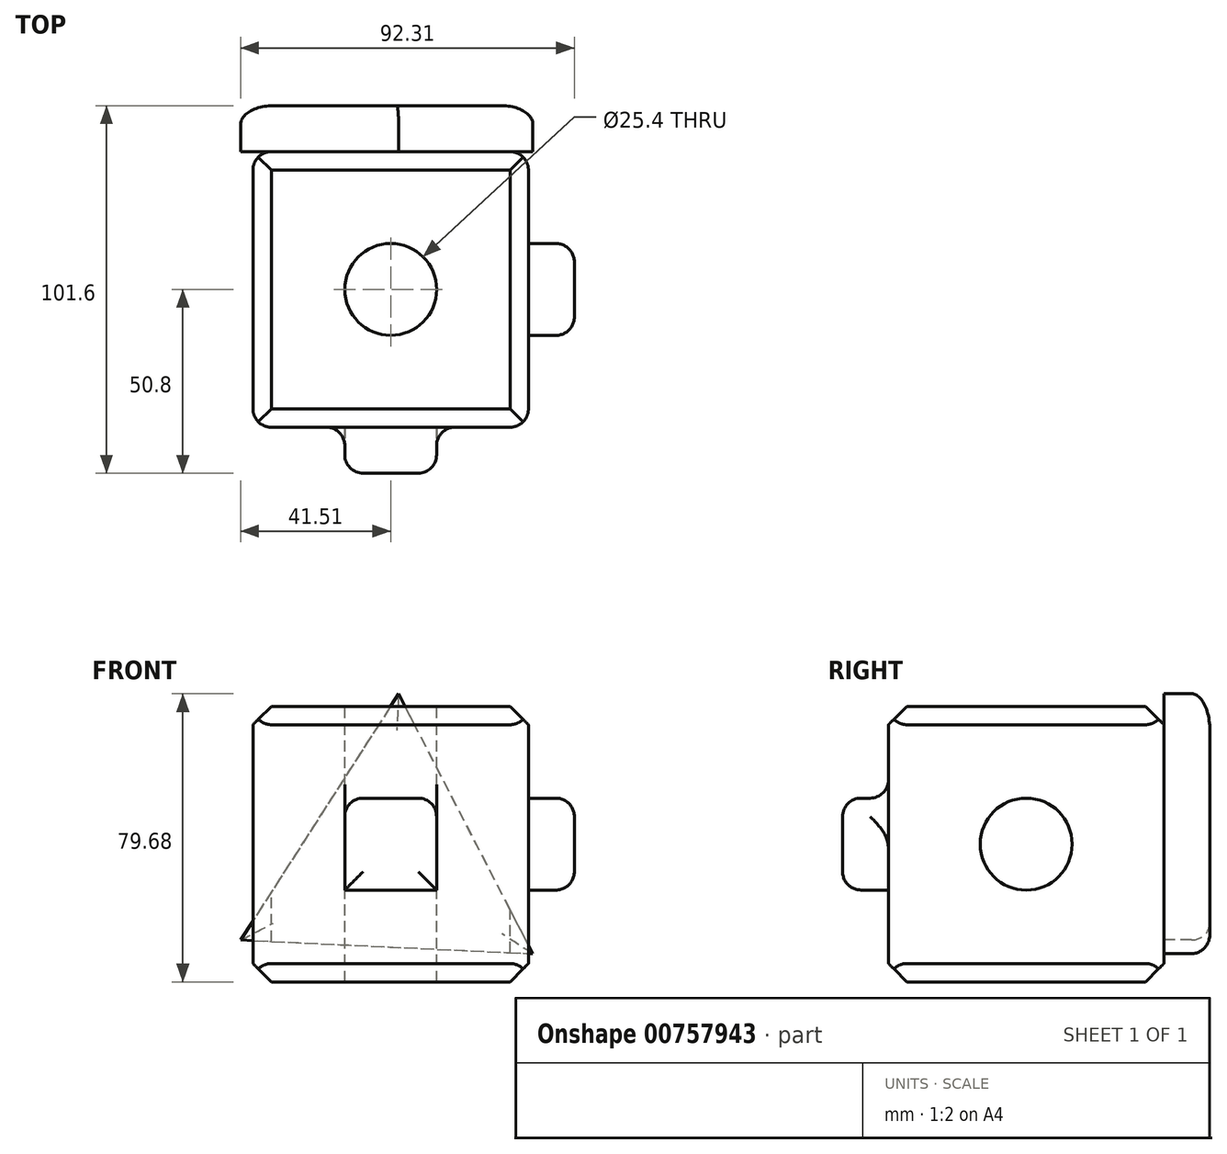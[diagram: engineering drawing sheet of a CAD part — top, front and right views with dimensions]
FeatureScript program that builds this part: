
annotation { "Feature Type Name" : "Feature", "Feature Type Description" : "" }
export const myFeature = defineFeature(function(context is Context, id is Id, definition is map)
    precondition{}
    {
        {
            var Q0;
            Q0=qCreatedBy(makeId("Front.planeOp"),FACE);
            var sketch = newSketch(context, id + "F0", { "sketchPlane" : qUnion([Q0])});
            skLineSegment(sketch, "E0.bottom", {"start": v(0, 32.56) * mm, "end": v(76.2, 32.56) * mm});
            skLineSegment(sketch, "E0.top", {"start": v(0, 108.76) * mm, "end": v(76.2, 108.76) * mm});
            skLineSegment(sketch, "E0.left", {"start": v(0, 32.56) * mm, "end": v(0, 108.76) * mm});
            skLineSegment(sketch, "E0.right", {"start": v(76.2, 32.56) * mm, "end": v(76.2, 108.76) * mm});
            skSolve(sketch);
        }
        {
            var Q0;
            Q0=makeQuery(id+"F0.imprint","IMPRINT",FACE,{"disambiguationData":[TD([[makeQuery(id+"F0.imprint","IMPRINT",EDGE,{"derivedFrom":sQuery(id+"F0.wireOp",EDGE,"E0.bottom")}),1.0]])]});
            extrude(context, id + "F1", {"entities" : qUnion([Q0]), "depth" : 76.2 * mm, "offsetDistance" : 25.4 * mm});
        }
        {
            var Q0;
            Q0=makeQuery(id+"F1.opExtrude","SWEPT_FACE",FACE,{"disambiguationData":[OSD([sQuery(id+"F0.wireOp",EDGE,"E0.top")])]});
            var sketch = newSketch(context, id + "F2", { "sketchPlane" : qUnion([Q0])});
            skPoint(sketch, "E1", {"position": v(38.1, -38.1) * mm});
            skSolve(sketch);
        }
        {
            var Q0;
            Q0=sQuery(id+"F2.wireOp",VERTEX,"E1");
            var Q1;
            Q1=makeQuery(id+"F1.opExtrude","SWEPT_BODY",BODY,{"disambiguationData":[OSD([sQuery(id+"F0.wireOp",EDGE,"E0.bottom"),sQuery(id+"F0.wireOp",EDGE,"E0.top"),sQuery(id+"F0.wireOp",EDGE,"E0.left"),sQuery(id+"F0.wireOp",EDGE,"E0.right")])]});
            hole(context, id + "F3", {"style" : HoleStyle.SIMPLE, "endStyle" : HoleEndStyle.THROUGH, "holeDiameter" : 25.4 * mm, "majorDiameter" : 6.35 * mm, "isTappedThrough" : true, "tappedDepth" : 12.7 * mm, "tapClearance" : 3, "locations" : qUnion([Q0]), "scope" : qUnion([Q1])});
        }
        {
            var Q0;
            Q0=makeQuery(id+"F1.opExtrude","CAP_FACE",FACE,{"disambiguationData":[OSD([sQuery(id+"F0.wireOp",EDGE,"E0.bottom"),sQuery(id+"F0.wireOp",EDGE,"E0.top"),sQuery(id+"F0.wireOp",EDGE,"E0.left"),sQuery(id+"F0.wireOp",EDGE,"E0.right")])],"isStart":false});
            var sketch = newSketch(context, id + "F4", { "sketchPlane" : qUnion([Q0])});
            skPoint(sketch, "E2", {"position": v(38.1, 70.66) * mm});
            skLineSegment(sketch, "E3.bottom", {"start": v(25.4, 83.36) * mm, "end": v(50.8, 83.36) * mm});
            skLineSegment(sketch, "E3.top", {"start": v(25.4, 57.96) * mm, "end": v(50.8, 57.96) * mm});
            skLineSegment(sketch, "E3.left", {"start": v(25.4, 83.36) * mm, "end": v(25.4, 57.96) * mm});
            skLineSegment(sketch, "E3.right", {"start": v(50.8, 83.36) * mm, "end": v(50.8, 57.96) * mm});
            skSolve(sketch);
        }
        {
            var Q0;
            Q0 = qSketchRegion(id + "F4", true);
            extrude(context, id + "F5", {"entities" : qUnion([Q0]), "operationType" : NewBodyOperationType.ADD, "depth" : 12.7 * mm, "offsetDistance" : 25.4 * mm});
        }
        {
            var Q0;
            Q0=makeQuery(id+"F1.opExtrude","SWEPT_FACE",FACE,{"disambiguationData":[OSD([sQuery(id+"F0.wireOp",EDGE,"E0.right")])]});
            var sketch = newSketch(context, id + "F6", { "sketchPlane" : qUnion([Q0])});
            skPoint(sketch, "E4", {"position": v(-38.1, 70.66) * mm});
            skCircle(sketch, "E5", {"center": v(-38.1, 70.66) * mm, "radius": 12.7 * mm});
            skSolve(sketch);
        }
        {
            var Q0;
            Q0 = qSketchRegion(id + "F6", true);
            extrude(context, id + "F7", {"entities" : qUnion([Q0]), "operationType" : NewBodyOperationType.ADD, "depth" : 12.7 * mm, "offsetDistance" : 25.4 * mm});
        }
        {
            var Q0;
            Q0=makeQuery(id+"F1.opExtrude","CAP_EDGE",EDGE,{"disambiguationData":[OSD([sQuery(id+"F0.wireOp",EDGE,"E0.top")])],"isStart":false});
            var Q1;
            Q1=makeQuery(id+"F1.opExtrude","SWEPT_EDGE",EDGE,{"disambiguationData":[OSD([sQuery(id+"F0.wireOp",EDGE,"E0.top"),sQuery(id+"F0.wireOp",EDGE,"E0.left")])]});
            var Q2;
            Q2=makeQuery(id+"F1.opExtrude","CAP_EDGE",EDGE,{"disambiguationData":[OSD([sQuery(id+"F0.wireOp",EDGE,"E0.top")])],"isStart":true});
            var Q3;
            Q3=makeQuery(id+"F1.opExtrude","SWEPT_EDGE",EDGE,{"disambiguationData":[OSD([sQuery(id+"F0.wireOp",EDGE,"E0.top"),sQuery(id+"F0.wireOp",EDGE,"E0.right")])]});
            var Q4;
            Q4=makeQuery(id+"F1.opExtrude","SWEPT_EDGE",EDGE,{"disambiguationData":[OSD([sQuery(id+"F0.wireOp",EDGE,"E0.bottom"),sQuery(id+"F0.wireOp",EDGE,"E0.right")])]});
            var Q5;
            Q5=makeQuery(id+"F1.opExtrude","CAP_EDGE",EDGE,{"disambiguationData":[OSD([sQuery(id+"F0.wireOp",EDGE,"E0.bottom")])],"isStart":false});
            var Q6;
            Q6=makeQuery(id+"F1.opExtrude","CAP_EDGE",EDGE,{"disambiguationData":[OSD([sQuery(id+"F0.wireOp",EDGE,"E0.bottom")])],"isStart":true});
            var Q7;
            Q7=makeQuery(id+"F1.opExtrude","SWEPT_EDGE",EDGE,{"disambiguationData":[OSD([sQuery(id+"F0.wireOp",EDGE,"E0.bottom"),sQuery(id+"F0.wireOp",EDGE,"E0.left")])]});
            chamfer(context, id + "F8", {"entities" : qUnion([Q0, Q1, Q2, Q3, Q4, Q5, Q6, Q7]), "width" : 5.08 * mm, "tangentPropagation" : true});
        }
        {
            var Q0;
            Q0=makeQuery(id+"F1.opExtrude","CAP_EDGE",EDGE,{"disambiguationData":[OSD([sQuery(id+"F0.wireOp",EDGE,"E0.left")])],"isStart":true});
            var Q1;
            Q1=makeQuery(id+"F1.opExtrude","CAP_EDGE",EDGE,{"disambiguationData":[OSD([sQuery(id+"F0.wireOp",EDGE,"E0.right")])],"isStart":true});
            var Q2;
            Q2=makeQuery(id+"F1.opExtrude","CAP_EDGE",EDGE,{"disambiguationData":[OSD([sQuery(id+"F0.wireOp",EDGE,"E0.left")])],"isStart":false});
            var Q3;
            Q3=makeQuery(id+"F1.opExtrude","CAP_EDGE",EDGE,{"disambiguationData":[OSD([sQuery(id+"F0.wireOp",EDGE,"E0.right")])],"isStart":false});
            var Q4;
            Q4=makeQuery(id+"F5.opExtrude","SWEPT_FACE",FACE,{"disambiguationData":[OSD([sQuery(id+"F4.wireOp",EDGE,"E3.bottom")])]});
            var Q5;
            Q5=makeQuery(id+"F5.opExtrude","CAP_FACE",FACE,{"disambiguationData":[OSD([sQuery(id+"F4.wireOp",EDGE,"E3.bottom"),sQuery(id+"F4.wireOp",EDGE,"E3.top"),sQuery(id+"F4.wireOp",EDGE,"E3.left"),sQuery(id+"F4.wireOp",EDGE,"E3.right")])],"isStart":false});
            var Q6;
            Q6=makeQuery(id+"F7.opExtrude","CAP_EDGE",EDGE,{"disambiguationData":[OSD([sQuery(id+"F6.wireOp",EDGE,"E5")])],"isStart":true});
            var Q7;
            Q7=makeQuery(id+"F7.opExtrude","CAP_EDGE",EDGE,{"disambiguationData":[OSD([sQuery(id+"F6.wireOp",EDGE,"E5")])],"isStart":false});
            var Q8;
            Q8=makeQuery(id+"F3.hole-0.boolean.opBoolean","COPY",FACE,{"derivedFrom":makeQuery(id+"F3.hole-0.opRevolve","SWEPT_FACE",FACE,{"disambiguationData":[OSD([sQuery(id+"F3.hole-0.sketch.wireOp",EDGE,"core_line_2")])]})});
            var Q9;
            Q9=makeQuery(id+"F3.hole-0.boolean.opBoolean","COPY",EDGE,{"derivedFrom":makeQuery(id+"F3.hole-0.opRevolve","SWEPT_EDGE",EDGE,{"disambiguationData":[OSD([sQuery(id+"F3.hole-0.sketch.wireOp",EDGE,"core_line_2"),sQuery(id+"F3.hole-0.sketch.wireOp",EDGE,"core_line_3")])]})});
            fillet(context, id + "F9", {"entities" : qUnion([Q0, Q1, Q2, Q3, Q4, Q5, Q6, Q7, Q8, Q9]), "radius" : 5.08 * mm, "tangentPropagation" : true, "allowEdgeOverflow" : false});
        }
        {
            var Q0;
            Q0=makeQuery(id+"F1.opExtrude","CAP_FACE",FACE,{"disambiguationData":[OSD([sQuery(id+"F0.wireOp",EDGE,"E0.bottom"),sQuery(id+"F0.wireOp",EDGE,"E0.top"),sQuery(id+"F0.wireOp",EDGE,"E0.left"),sQuery(id+"F0.wireOp",EDGE,"E0.right")])],"isStart":true});
            var sketch = newSketch(context, id + "F10", { "sketchPlane" : qUnion([Q0])});
            skPoint(sketch, "E6", {"position": v(-38.1, 65.58) * mm});
            skCircle(sketch, "E7.cCircle", {"center": v(-38.1, 65.58) * mm, "radius": 23.36 * mm, "construction": true});
            skLineSegment(sketch, "E7.0", {"start": v(-77.42, 40.35) * mm, "end": v(-40.29, 112.24) * mm});
            skLineSegment(sketch, "E7.1", {"start": v(-40.29, 112.24) * mm, "end": v(3.4, 44.14) * mm});
            skLineSegment(sketch, "E7.2", {"start": v(3.4, 44.14) * mm, "end": v(-77.42, 40.35) * mm});
            skPoint(sketch, "E7.0.midPoint", {"position": v(-58.85, 76.3) * mm});
            skSolve(sketch);
        }
        {
            var Q0;
            Q0 = qSketchRegion(id + "F10", true);
            extrude(context, id + "F11", {"entities" : qUnion([Q0]), "operationType" : NewBodyOperationType.ADD, "depth" : 12.7 * mm, "offsetDistance" : 25.4 * mm});
        }
        {
            var Q0;
            Q0=makeQuery(id+"F11.opExtrude","CAP_FACE",FACE,{"disambiguationData":[OSD([sQuery(id+"F10.wireOp",EDGE,"E7.0"),sQuery(id+"F10.wireOp",EDGE,"E7.1"),sQuery(id+"F10.wireOp",EDGE,"E7.2")])],"isStart":false});
            fillet(context, id + "F12", {"entities" : qUnion([Q0]), "radius" : 5.08 * mm, "tangentPropagation" : true, "allowEdgeOverflow" : false});
        }
    });
